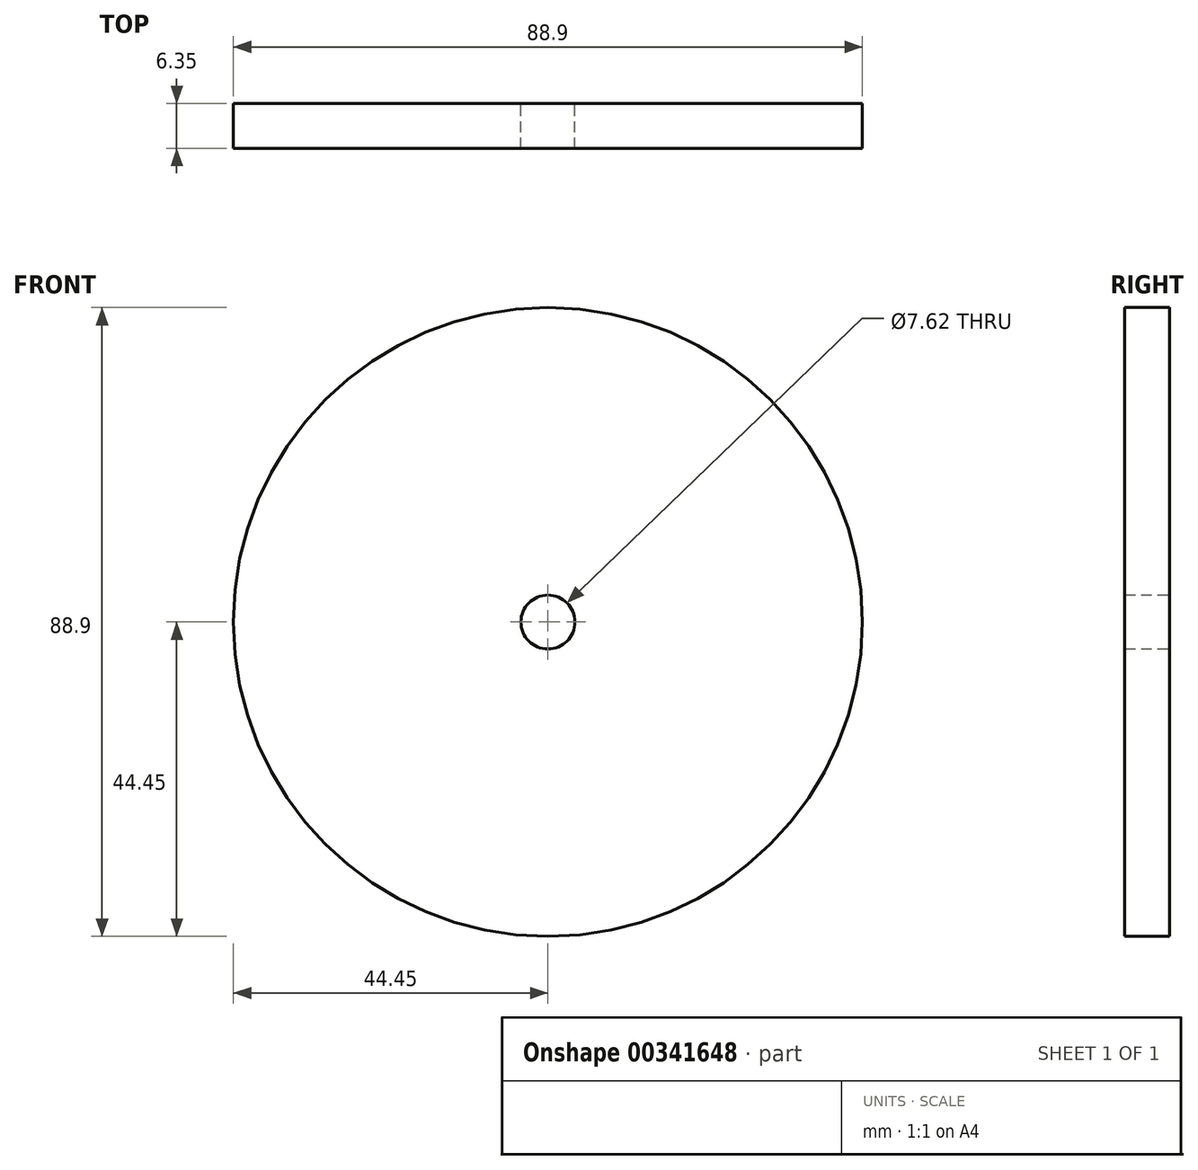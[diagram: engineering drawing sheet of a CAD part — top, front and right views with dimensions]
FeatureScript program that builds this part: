
annotation { "Feature Type Name" : "Feature", "Feature Type Description" : "" }
export const myFeature = defineFeature(function(context is Context, id is Id, definition is map)
    precondition{}
    {
        {
            var Q0;
            Q0=qCreatedBy(makeId("Front.planeOp"),FACE);
            var sketch = newSketch(context, id + "F0", { "sketchPlane" : qUnion([Q0])});
            skCircle(sketch, "E0", {"center": v(0, 0) * mm, "radius": 44.45 * mm});
            skCircle(sketch, "E1", {"center": v(0, 0) * mm, "radius": 3.81 * mm});
            skSolve(sketch);
        }
        {
            var Q0;
            Q0=makeQuery(id+"F0.imprint","IMPRINT",FACE,{"disambiguationData":[TD([[makeQuery(id+"F0.imprint","IMPRINT",EDGE,{"derivedFrom":sQuery(id+"F0.wireOp",EDGE,"E0")}),1.0]])]});
            extrude(context, id + "F1", {"entities" : qUnion([Q0]), "depth" : 6.35 * mm});
        }
    });
